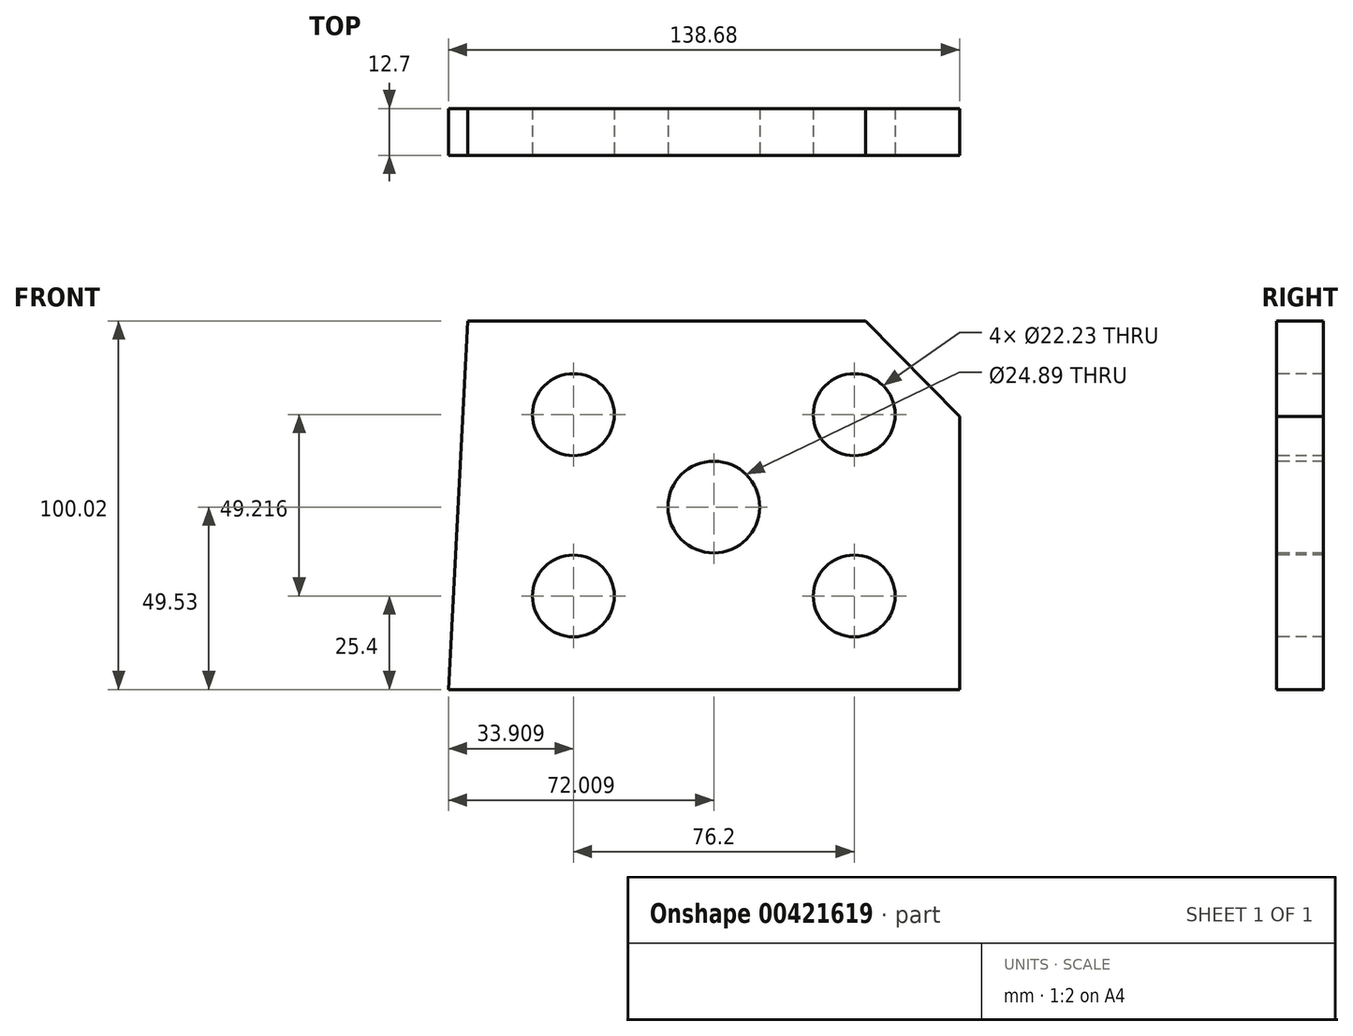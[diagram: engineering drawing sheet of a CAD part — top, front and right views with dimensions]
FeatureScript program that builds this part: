
annotation { "Feature Type Name" : "Feature", "Feature Type Description" : "" }
export const myFeature = defineFeature(function(context is Context, id is Id, definition is map)
    precondition{}
    {
        {
            var Q0;
            Q0=qCreatedBy(makeId("Front.planeOp"),FACE);
            var sketch = newSketch(context, id + "F0", { "sketchPlane" : qUnion([Q0])});
            skLineSegment(sketch, "E0", {"start": v(0, 0) * mm, "end": v(138.68, 0) * mm});
            skLineSegment(sketch, "E1", {"start": v(138.68, 0) * mm, "end": v(138.68, 74.17) * mm});
            skLineSegment(sketch, "E2", {"start": v(0, 0) * mm, "end": v(5.22, 100.02) * mm});
            skLineSegment(sketch, "E3", {"start": v(5.22, 100.02) * mm, "end": v(113.17, 100.02) * mm});
            skLineSegment(sketch, "E4", {"start": v(113.17, 100.02) * mm, "end": v(138.68, 74.17) * mm});
            skSolve(sketch);
        }
        {
            var Q0;
            Q0 = qSketchRegion(id + "F0", true);
            extrude(context, id + "F1", {"entities" : qUnion([Q0]), "depth" : 12.7 * mm});
        }
        {
            var Q0;
            Q0=makeQuery(id+"F1.opExtrude","CAP_FACE",FACE,{"disambiguationData":[OSD([sQuery(id+"F0.wireOp",EDGE,"E0"),sQuery(id+"F0.wireOp",EDGE,"E1"),sQuery(id+"F0.wireOp",EDGE,"E2"),sQuery(id+"F0.wireOp",EDGE,"E3"),sQuery(id+"F0.wireOp",EDGE,"E4")])],"isStart":false});
            var sketch = newSketch(context, id + "F2", { "sketchPlane" : qUnion([Q0])});
            skLineSegment(sketch, "E5", {"start": v(138.68, 25.4) * mm, "end": v(110.1, 25.4) * mm, "construction": true});
            skLineSegment(sketch, "E6", {"start": v(110.1, 25.4) * mm, "end": v(110.1, 74.62) * mm, "construction": true});
            skLineSegment(sketch, "E7", {"start": v(138.68, 74.62) * mm, "end": v(33.9, 74.62) * mm, "construction": true});
            skLineSegment(sketch, "E8", {"start": v(33.9, 74.62) * mm, "end": v(33.9, 25.4) * mm, "construction": true});
            skLineSegment(sketch, "E9", {"start": v(138.68, 49.53) * mm, "end": v(72, 49.53) * mm, "construction": true});
            skCircle(sketch, "E10", {"center": v(72, 49.53) * mm, "radius": 12.45 * mm});
            skCircle(sketch, "E11", {"center": v(33.9, 25.4) * mm, "radius": 11.11 * mm});
            skCircle(sketch, "E12", {"center": v(33.9, 74.62) * mm, "radius": 11.11 * mm});
            skCircle(sketch, "E13", {"center": v(110.1, 74.62) * mm, "radius": 11.11 * mm});
            skCircle(sketch, "E14", {"center": v(110.1, 25.4) * mm, "radius": 11.11 * mm});
            skSolve(sketch);
        }
        {
            var Q0;
            Q0 = qSketchRegion(id + "F2", true);
            extrude(context, id + "F3", {"entities" : qUnion([Q0]), "operationType" : NewBodyOperationType.REMOVE, "oppositeDirection" : true, "depth" : 25.4 * mm});
        }
    });
